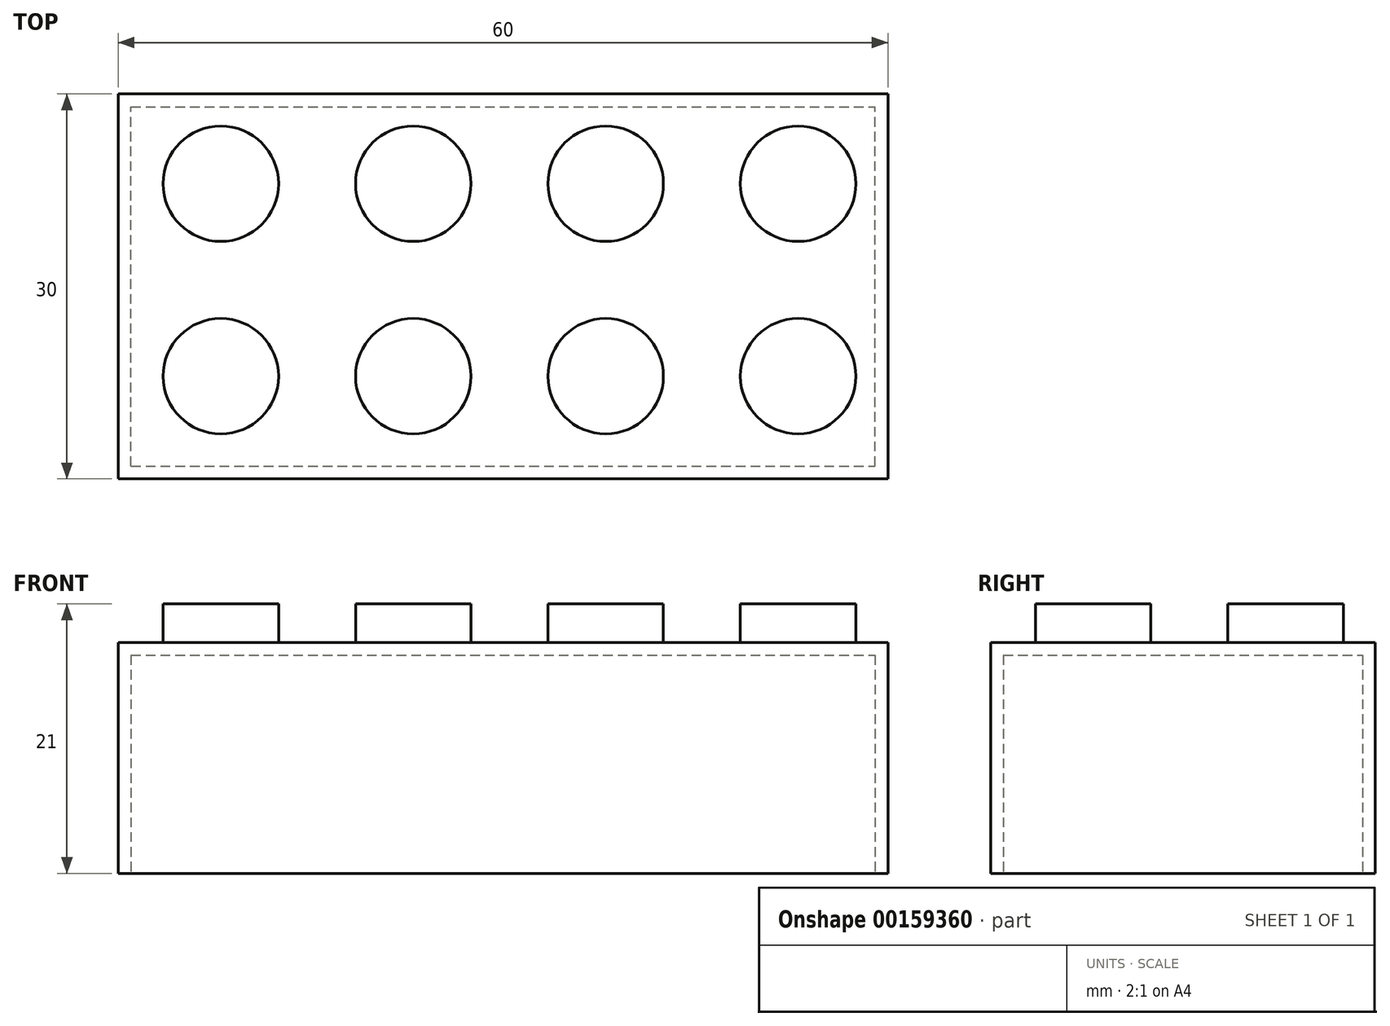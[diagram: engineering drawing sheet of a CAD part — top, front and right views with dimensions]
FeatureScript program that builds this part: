
annotation { "Feature Type Name" : "Feature", "Feature Type Description" : "" }
export const myFeature = defineFeature(function(context is Context, id is Id, definition is map)
    precondition{}
    {
        {
            var Q0;
            Q0=qCreatedBy(makeId("Top.planeOp"),FACE);
            var sketch = newSketch(context, id + "F0", { "sketchPlane" : qUnion([Q0])});
            skLineSegment(sketch, "E0.bottom", {"start": v(0, 0) * mm, "end": v(60, 0) * mm});
            skLineSegment(sketch, "E0.top", {"start": v(0, 30) * mm, "end": v(60, 30) * mm});
            skLineSegment(sketch, "E0.left", {"start": v(0, 0) * mm, "end": v(0, 30) * mm});
            skLineSegment(sketch, "E0.right", {"start": v(60, 0) * mm, "end": v(60, 30) * mm});
            skSolve(sketch);
        }
        {
            var Q0;
            Q0=makeQuery(id+"F0.imprint","IMPRINT",FACE,{"disambiguationData":[TD([[makeQuery(id+"F0.imprint","IMPRINT",EDGE,{"derivedFrom":sQuery(id+"F0.wireOp",EDGE,"E0.bottom")}),1.0]])]});
            extrude(context, id + "F1", {"entities" : qUnion([Q0]), "depth" : 18 * mm});
        }
        {
            var Q0;
            Q0=makeQuery(id+"F1.opExtrude","CAP_FACE",FACE,{"disambiguationData":[OSD([sQuery(id+"F0.wireOp",EDGE,"E0.bottom"),sQuery(id+"F0.wireOp",EDGE,"E0.top"),sQuery(id+"F0.wireOp",EDGE,"E0.left"),sQuery(id+"F0.wireOp",EDGE,"E0.right")])],"isStart":true});
            shell(context, id + "F2", {"entities" : qUnion([Q0]), "thickness" : 1 * mm});
        }
        {
            var Q0;
            Q0=makeQuery(id+"F1.opExtrude","CAP_FACE",FACE,{"disambiguationData":[OSD([sQuery(id+"F0.wireOp",EDGE,"E0.bottom"),sQuery(id+"F0.wireOp",EDGE,"E0.top"),sQuery(id+"F0.wireOp",EDGE,"E0.left"),sQuery(id+"F0.wireOp",EDGE,"E0.right")])],"isStart":false});
            var sketch = newSketch(context, id + "F3", { "sketchPlane" : qUnion([Q0])});
            skCircle(sketch, "E1", {"center": v(53, 23) * mm, "radius": 4.5 * mm});
            skCircle(sketch, "E2.0.1.0", {"center": v(53, 8) * mm, "radius": 4.5 * mm});
            skCircle(sketch, "E2.1.0.0", {"center": v(38, 23) * mm, "radius": 4.5 * mm});
            skCircle(sketch, "E2.1.1.0", {"center": v(38, 8) * mm, "radius": 4.5 * mm});
            skCircle(sketch, "E2.2.0.0", {"center": v(23, 23) * mm, "radius": 4.5 * mm});
            skCircle(sketch, "E2.2.1.0", {"center": v(23, 8) * mm, "radius": 4.5 * mm});
            skCircle(sketch, "E2.3.0.0", {"center": v(8, 23) * mm, "radius": 4.5 * mm});
            skCircle(sketch, "E2.3.1.0", {"center": v(8, 8) * mm, "radius": 4.5 * mm});
            skLineSegment(sketch, "E2.direction1", {"start": v(53, 23) * mm, "end": v(38, 23) * mm, "construction": true});
            skLineSegment(sketch, "E2.direction2", {"start": v(53, 23) * mm, "end": v(53, 8) * mm, "construction": true});
            skSolve(sketch);
        }
        {
            var Q0;
            Q0=makeQuery(id+"F3.imprint","IMPRINT",FACE,{"disambiguationData":[TD([[makeQuery(id+"F3.imprint","IMPRINT",EDGE,{"derivedFrom":sQuery(id+"F3.wireOp",EDGE,"E2.3.1.0")}),1.0]])]});
            var Q1;
            Q1=makeQuery(id+"F3.imprint","IMPRINT",FACE,{"disambiguationData":[TD([[makeQuery(id+"F3.imprint","IMPRINT",EDGE,{"derivedFrom":sQuery(id+"F3.wireOp",EDGE,"E2.2.1.0")}),1.0]])]});
            var Q2;
            Q2=makeQuery(id+"F3.imprint","IMPRINT",FACE,{"disambiguationData":[TD([[makeQuery(id+"F3.imprint","IMPRINT",EDGE,{"derivedFrom":sQuery(id+"F3.wireOp",EDGE,"E2.3.0.0")}),1.0]])]});
            var Q3;
            Q3=makeQuery(id+"F3.imprint","IMPRINT",FACE,{"disambiguationData":[TD([[makeQuery(id+"F3.imprint","IMPRINT",EDGE,{"derivedFrom":sQuery(id+"F3.wireOp",EDGE,"E2.2.0.0")}),1.0]])]});
            var Q4;
            Q4=makeQuery(id+"F3.imprint","IMPRINT",FACE,{"disambiguationData":[TD([[makeQuery(id+"F3.imprint","IMPRINT",EDGE,{"derivedFrom":sQuery(id+"F3.wireOp",EDGE,"E2.1.0.0")}),1.0]])]});
            var Q5;
            Q5=makeQuery(id+"F3.imprint","IMPRINT",FACE,{"disambiguationData":[TD([[makeQuery(id+"F3.imprint","IMPRINT",EDGE,{"derivedFrom":sQuery(id+"F3.wireOp",EDGE,"E2.0.1.0")}),1.0]])]});
            var Q6;
            Q6=makeQuery(id+"F3.imprint","IMPRINT",FACE,{"disambiguationData":[TD([[makeQuery(id+"F3.imprint","IMPRINT",EDGE,{"derivedFrom":sQuery(id+"F3.wireOp",EDGE,"E2.1.1.0")}),1.0]])]});
            var Q7;
            Q7=makeQuery(id+"F3.imprint","IMPRINT",FACE,{"disambiguationData":[TD([[makeQuery(id+"F3.imprint","IMPRINT",EDGE,{"derivedFrom":sQuery(id+"F3.wireOp",EDGE,"E1")}),1.0]])]});
            extrude(context, id + "F4", {"entities" : qUnion([Q0, Q1, Q2, Q3, Q4, Q5, Q6, Q7]), "operationType" : NewBodyOperationType.ADD, "depth" : 3 * mm});
        }
    });
